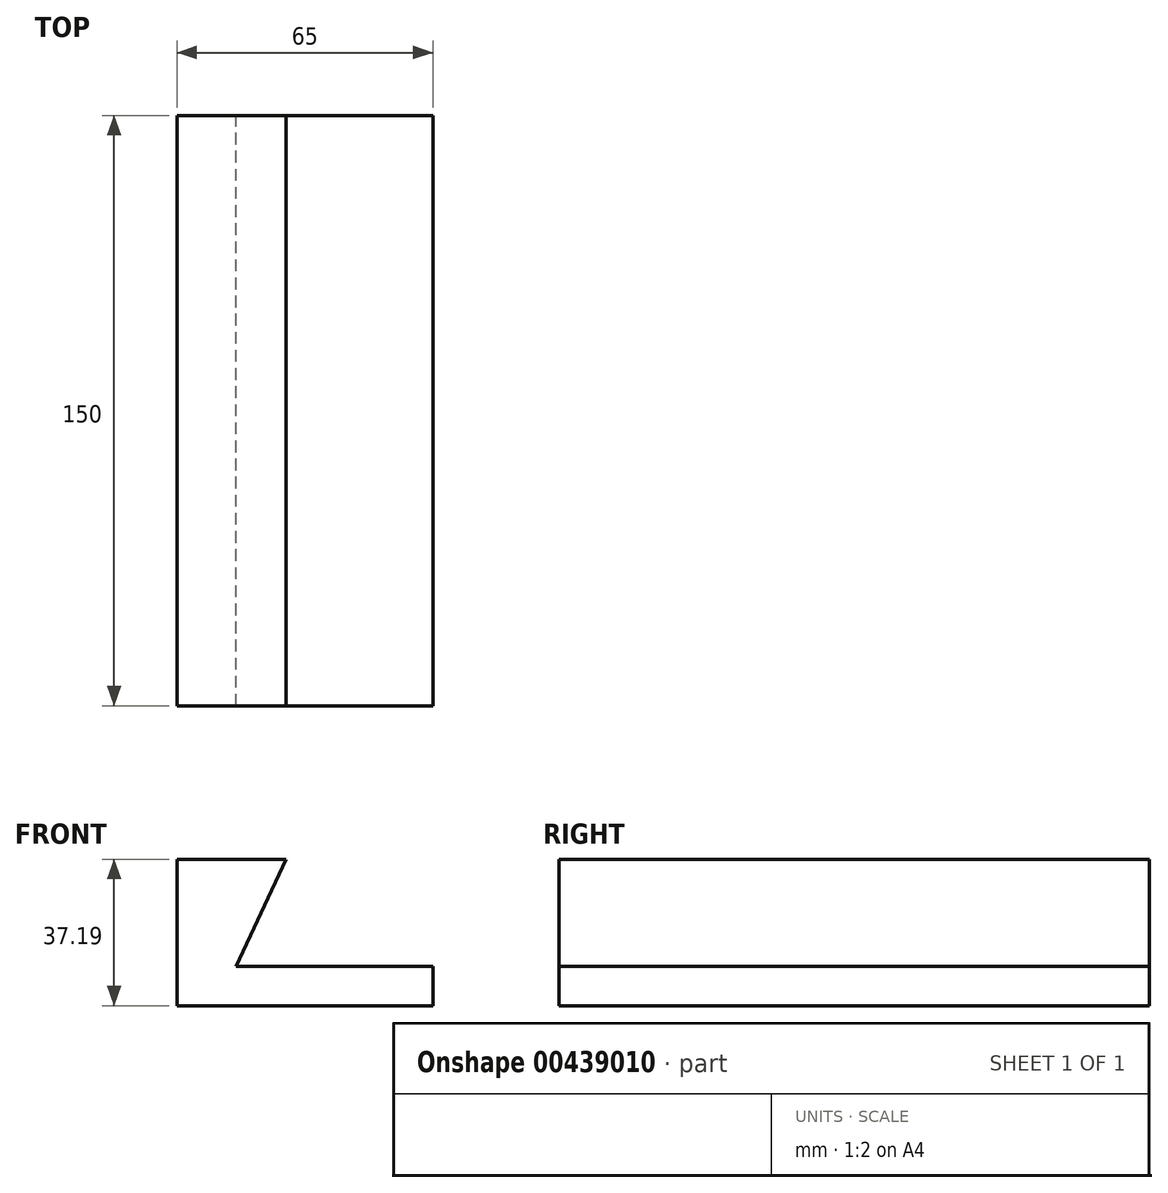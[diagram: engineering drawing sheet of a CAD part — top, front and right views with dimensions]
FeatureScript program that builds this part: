
annotation { "Feature Type Name" : "Feature", "Feature Type Description" : "" }
export const myFeature = defineFeature(function(context is Context, id is Id, definition is map)
    precondition{}
    {
        {
            assignVariable(context, id + "F0", {"name" : "Longueur", "anyValue" : 150 * mm});
        }
        {
            var Q0;
            Q0=qCreatedBy(makeId("Front.planeOp"),FACE);
            var sketch = newSketch(context, id + "F1", { "sketchPlane" : qUnion([Q0])});
            skLineSegment(sketch, "E0", {"start": v(0, 0) * mm, "end": v(50, 0) * mm});
            skLineSegment(sketch, "E1", {"start": v(0, 0) * mm, "end": v(12.68, 27.19) * mm});
            skLineSegment(sketch, "E2", {"start": v(12.68, 27.19) * mm, "end": v(-15, 27.19) * mm});
            skLineSegment(sketch, "E3", {"start": v(-15, 27.19) * mm, "end": v(-15, -10) * mm});
            skLineSegment(sketch, "E4", {"start": v(-15, -10) * mm, "end": v(50, -10) * mm});
            skLineSegment(sketch, "E5", {"start": v(50, -10) * mm, "end": v(50, 0) * mm});
            skSolve(sketch);
        }
        {
            var Q0;
            Q0=makeQuery(id+"F1.imprint","IMPRINT",FACE,{"disambiguationData":[TD([[makeQuery(id+"F1.imprint","IMPRINT",EDGE,{"derivedFrom":sQuery(id+"F1.wireOp",EDGE,"E0")}),-1.0]])]});
            extrude(context, id + "F2", {"entities" : qUnion([Q0]), "depth" : getVariable(context, 'Longueur')});
        }
    });
